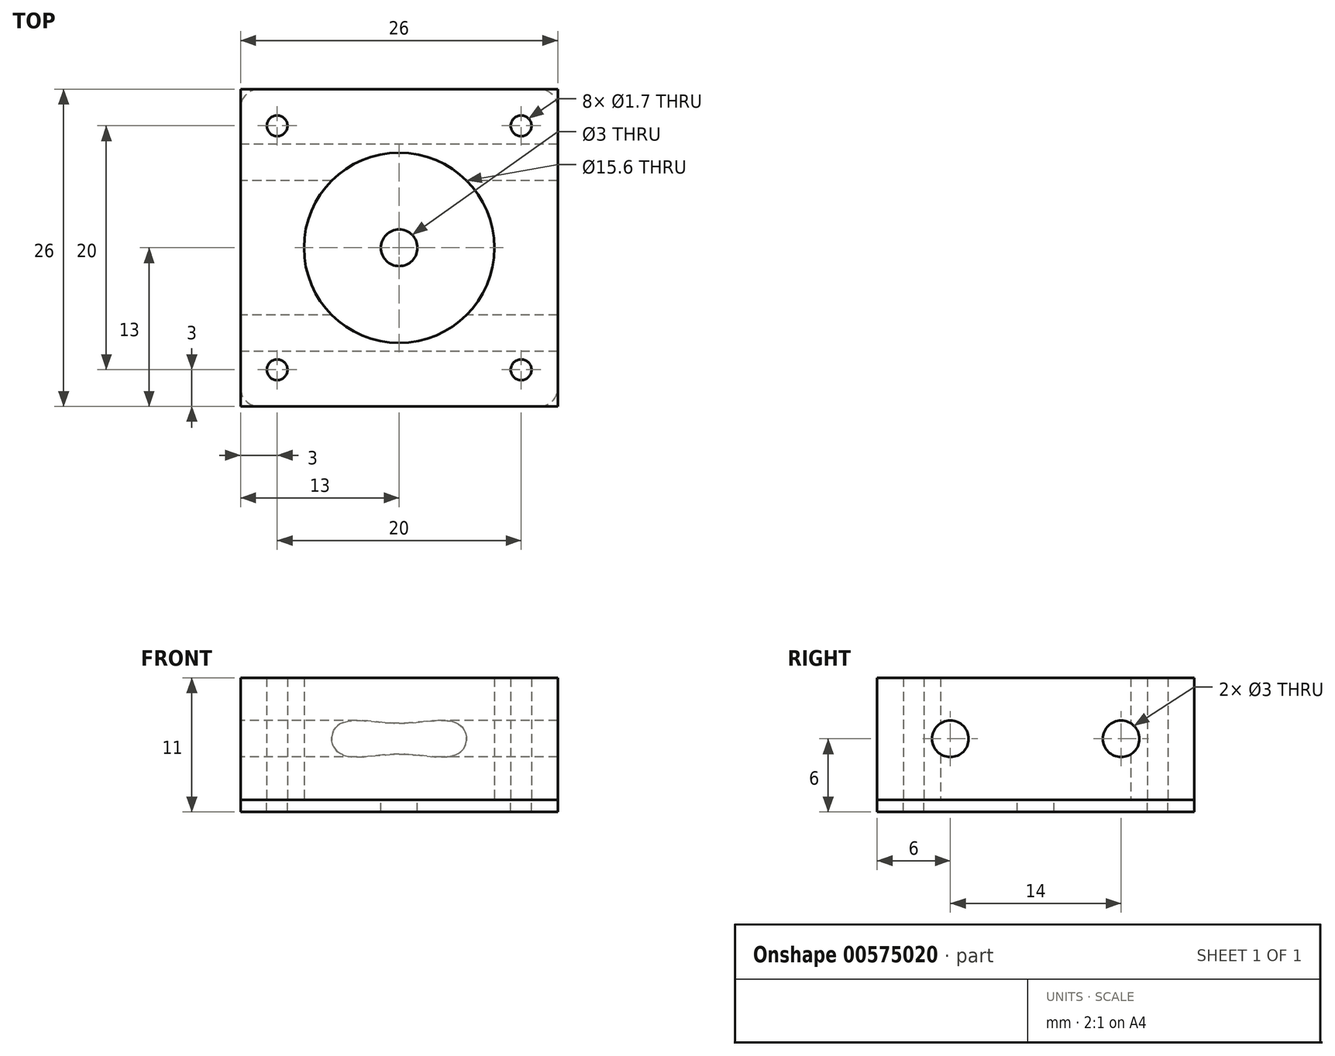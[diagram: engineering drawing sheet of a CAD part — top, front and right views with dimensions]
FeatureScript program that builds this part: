
annotation { "Feature Type Name" : "Feature", "Feature Type Description" : "" }
export const myFeature = defineFeature(function(context is Context, id is Id, definition is map)
    precondition{}
    {
        {
            var Q0;
            Q0=qCreatedBy(makeId("Top.planeOp"),FACE);
            var sketch = newSketch(context, id + "F0", { "sketchPlane" : qUnion([Q0])});
            skLineSegment(sketch, "E0.bottom", {"start": v(-13, 13) * mm, "end": v(13, 13) * mm});
            skLineSegment(sketch, "E0.top", {"start": v(-13, -13) * mm, "end": v(13, -13) * mm});
            skLineSegment(sketch, "E0.left", {"start": v(-13, 13) * mm, "end": v(-13, -13) * mm});
            skLineSegment(sketch, "E0.right", {"start": v(13, 13) * mm, "end": v(13, -13) * mm});
            skPoint(sketch, "E0.middle", {"position": v(0, 0) * mm});
            skCircle(sketch, "E1", {"center": v(0, 0) * mm, "radius": 7.8 * mm});
            skLineSegment(sketch, "E2.bottom", {"start": v(-10, 10) * mm, "end": v(10, 10) * mm, "construction": true});
            skLineSegment(sketch, "E2.top", {"start": v(-10, -10) * mm, "end": v(10, -10) * mm, "construction": true});
            skLineSegment(sketch, "E2.left", {"start": v(-10, 10) * mm, "end": v(-10, -10) * mm, "construction": true});
            skLineSegment(sketch, "E2.right", {"start": v(10, 10) * mm, "end": v(10, -10) * mm, "construction": true});
            skCircle(sketch, "E3", {"center": v(-10, 10) * mm, "radius": 0.85 * mm});
            skCircle(sketch, "E4.MirrorC", {"center": v(10, 10) * mm, "radius": 0.85 * mm});
            skCircle(sketch, "E5.MirrorC", {"center": v(-10, -10) * mm, "radius": 0.85 * mm});
            skCircle(sketch, "E6.MirrorC", {"center": v(10, -10) * mm, "radius": 0.85 * mm});
            skSolve(sketch);
        }
        {
            var Q0;
            Q0 = qSketchRegion(id + "F0", true);
            extrude(context, id + "F1", {"entities" : qUnion([Q0]), "depth" : 10 * mm, "offsetDistance" : 25 * mm});
        }
        {
            var Q0;
            Q0=makeQuery(id+"F1.opExtrude","SWEPT_FACE",FACE,{"disambiguationData":[OSD([sQuery(id+"F0.wireOp",EDGE,"E0.left")])]});
            var sketch = newSketch(context, id + "F2", { "sketchPlane" : qUnion([Q0])});
            skLineSegment(sketch, "E7", {"start": v(-13, 5) * mm, "end": v(13, 5) * mm, "construction": true});
            skCircle(sketch, "E8", {"center": v(-7, 5) * mm, "radius": 1.5 * mm});
            skCircle(sketch, "E9.MirrorC", {"center": v(7, 5) * mm, "radius": 1.5 * mm});
            skSolve(sketch);
        }
        {
            var Q0;
            Q0 = qSketchRegion(id + "F2", true);
            extrude(context, id + "F3", {"entities" : qUnion([Q0]), "operationType" : NewBodyOperationType.REMOVE, "endBound" : BoundingType.THROUGH_ALL, "oppositeDirection" : true, "depth" : 25 * mm, "offsetDistance" : 25 * mm});
        }
        {
            var Q0;
            Q0=makeQuery(id+"F1.opExtrude","CAP_FACE",FACE,{"disambiguationData":[OSD([sQuery(id+"F0.wireOp",EDGE,"E0.bottom"),sQuery(id+"F0.wireOp",EDGE,"E0.top"),sQuery(id+"F0.wireOp",EDGE,"E0.left"),sQuery(id+"F0.wireOp",EDGE,"E0.right"),sQuery(id+"F0.wireOp",EDGE,"E1"),sQuery(id+"F0.wireOp",EDGE,"E3"),sQuery(id+"F0.wireOp",EDGE,"E4.MirrorC"),sQuery(id+"F0.wireOp",EDGE,"E5.MirrorC"),sQuery(id+"F0.wireOp",EDGE,"E6.MirrorC")])],"isStart":true});
            var sketch = newSketch(context, id + "F4", { "sketchPlane" : qUnion([Q0])});
            skLineSegment(sketch, "E10.0.0", {"start": v(-13, 11.5) * mm, "end": v(-13, -11.5) * mm});
            skLineSegment(sketch, "E10.0.1", {"start": v(-11.5, -13) * mm, "end": v(11.5, -13) * mm});
            skLineSegment(sketch, "E10.0.2", {"start": v(13, -11.5) * mm, "end": v(13, 11.5) * mm});
            skLineSegment(sketch, "E10.0.3", {"start": v(11.5, 13) * mm, "end": v(-11.5, 13) * mm});
            skCircle(sketch, "E11.0", {"center": v(0, 0) * mm, "radius": 7.8 * mm});
            skCircle(sketch, "E12.0", {"center": v(10, -10) * mm, "radius": 0.85 * mm});
            skCircle(sketch, "E13.0", {"center": v(-10, -10) * mm, "radius": 0.85 * mm});
            skCircle(sketch, "E14.0", {"center": v(-10, 10) * mm, "radius": 0.85 * mm});
            skCircle(sketch, "E15.0", {"center": v(10, 10) * mm, "radius": 0.85 * mm});
            skCircle(sketch, "E16", {"center": v(0, 0) * mm, "radius": 1.5 * mm});
            skPoint(sketch, "E17.visualSharp", {"position": v(-13, 13) * mm});
            skArc(sketch, "E17.filletArc", {"start": v(-11.5, 13) * mm, "mid": v(-12.56, 12.56) * mm, "end": v(-13, 11.5) * mm});
            skPoint(sketch, "E18.visualSharp", {"position": v(13, 13) * mm});
            skArc(sketch, "E18.filletArc", {"start": v(13, 11.5) * mm, "mid": v(12.56, 12.56) * mm, "end": v(11.5, 13) * mm});
            skPoint(sketch, "E19.visualSharp", {"position": v(-13, -13) * mm});
            skArc(sketch, "E19.filletArc", {"start": v(-13, -11.5) * mm, "mid": v(-12.56, -12.56) * mm, "end": v(-11.5, -13) * mm});
            skPoint(sketch, "E20.visualSharp", {"position": v(13, -13) * mm});
            skArc(sketch, "E20.filletArc", {"start": v(11.5, -13) * mm, "mid": v(12.56, -12.56) * mm, "end": v(13, -11.5) * mm});
            skSolve(sketch);
        }
        {
            var Q0;
            Q0 = qSketchRegion(id + "F4", true);
            var Q1;
            Q1=makeQuery(id+"F4.imprint","IMPRINT",FACE,{"disambiguationData":[TD([[makeQuery(id+"F4.imprint","IMPRINT",EDGE,{"derivedFrom":sQuery(id+"F4.wireOp",EDGE,"E11.0")}),-1.0]])]});
            extrude(context, id + "F5", {"entities" : qUnion([Q0, Q1]), "depth" : 1 * mm, "offsetDistance" : 25 * mm});
        }
    });
